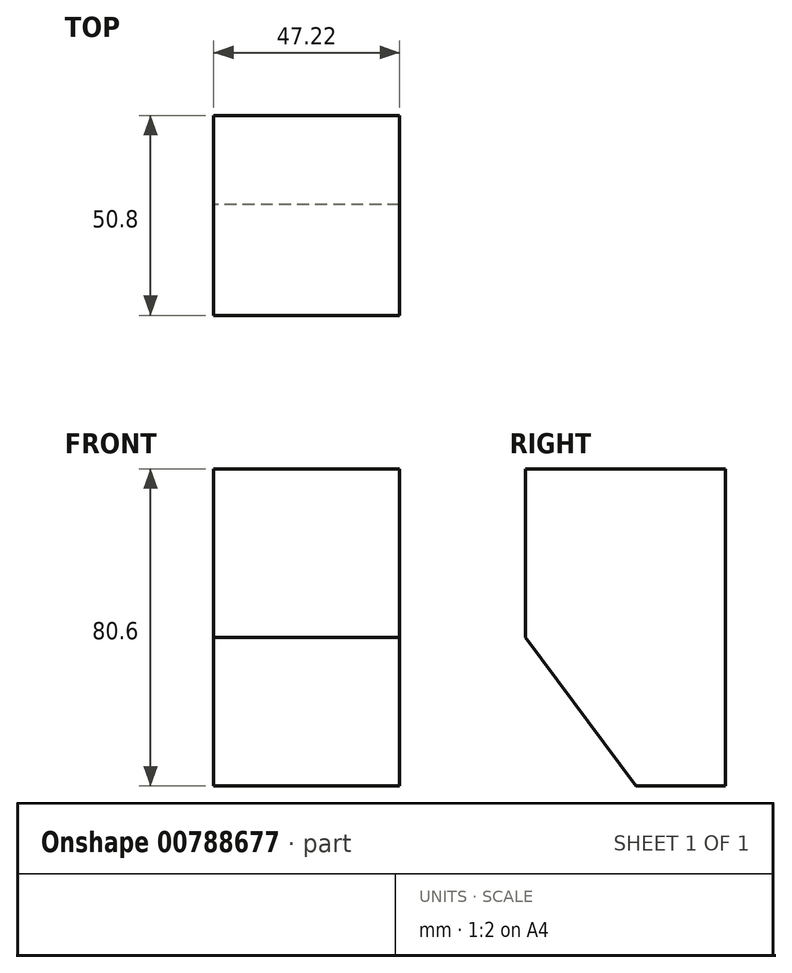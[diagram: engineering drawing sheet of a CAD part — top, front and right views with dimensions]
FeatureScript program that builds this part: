
annotation { "Feature Type Name" : "Feature", "Feature Type Description" : "" }
export const myFeature = defineFeature(function(context is Context, id is Id, definition is map)
    precondition{}
    {
        {
            var Q0;
            Q0=qCreatedBy(makeId("Front.planeOp"),FACE);
            var sketch = newSketch(context, id + "F0", { "sketchPlane" : qUnion([Q0])});
            skLineSegment(sketch, "E0.bottom", {"start": v(-23.6, 40.3) * mm, "end": v(23.6, 40.3) * mm});
            skLineSegment(sketch, "E0.top", {"start": v(-23.6, -40.3) * mm, "end": v(23.6, -40.3) * mm});
            skLineSegment(sketch, "E0.left", {"start": v(-23.6, 40.3) * mm, "end": v(-23.6, -40.3) * mm});
            skLineSegment(sketch, "E0.right", {"start": v(23.6, 40.3) * mm, "end": v(23.6, -40.3) * mm});
            skPoint(sketch, "E0.middle", {"position": v(0, 0) * mm});
            skSolve(sketch);
        }
        {
            var Q0;
            Q0 = qSketchRegion(id + "F0", true);
            extrude(context, id + "F1", {"entities" : qUnion([Q0]), "depth" : 50.8 * mm, "offsetDistance" : 25.4 * mm});
        }
        {
            var Q0;
            Q0=makeQuery(id+"F1.opExtrude","SWEPT_FACE",FACE,{"disambiguationData":[OSD([sQuery(id+"F0.wireOp",EDGE,"E0.left")])]});
            var sketch = newSketch(context, id + "F2", { "sketchPlane" : qUnion([Q0])});
            skLineSegment(sketch, "E1", {"start": v(50.8, -2.57) * mm, "end": v(16.24, -48.97) * mm});
            skLineSegment(sketch, "E2", {"start": v(16.24, -48.97) * mm, "end": v(63.08, -48.97) * mm});
            skLineSegment(sketch, "E3", {"start": v(63.08, -48.97) * mm, "end": v(59.44, 1.7) * mm});
            skLineSegment(sketch, "E4", {"start": v(59.44, 1.7) * mm, "end": v(50.8, -2.57) * mm});
            skSolve(sketch);
        }
        {
            var Q0;
            Q0 = qSketchRegion(id + "F2", true);
            extrude(context, id + "F3", {"entities" : qUnion([Q0]), "operationType" : NewBodyOperationType.REMOVE, "endBound" : BoundingType.THROUGH_ALL, "oppositeDirection" : true, "depth" : 25.4 * mm, "offsetDistance" : 25.4 * mm});
        }
    });
